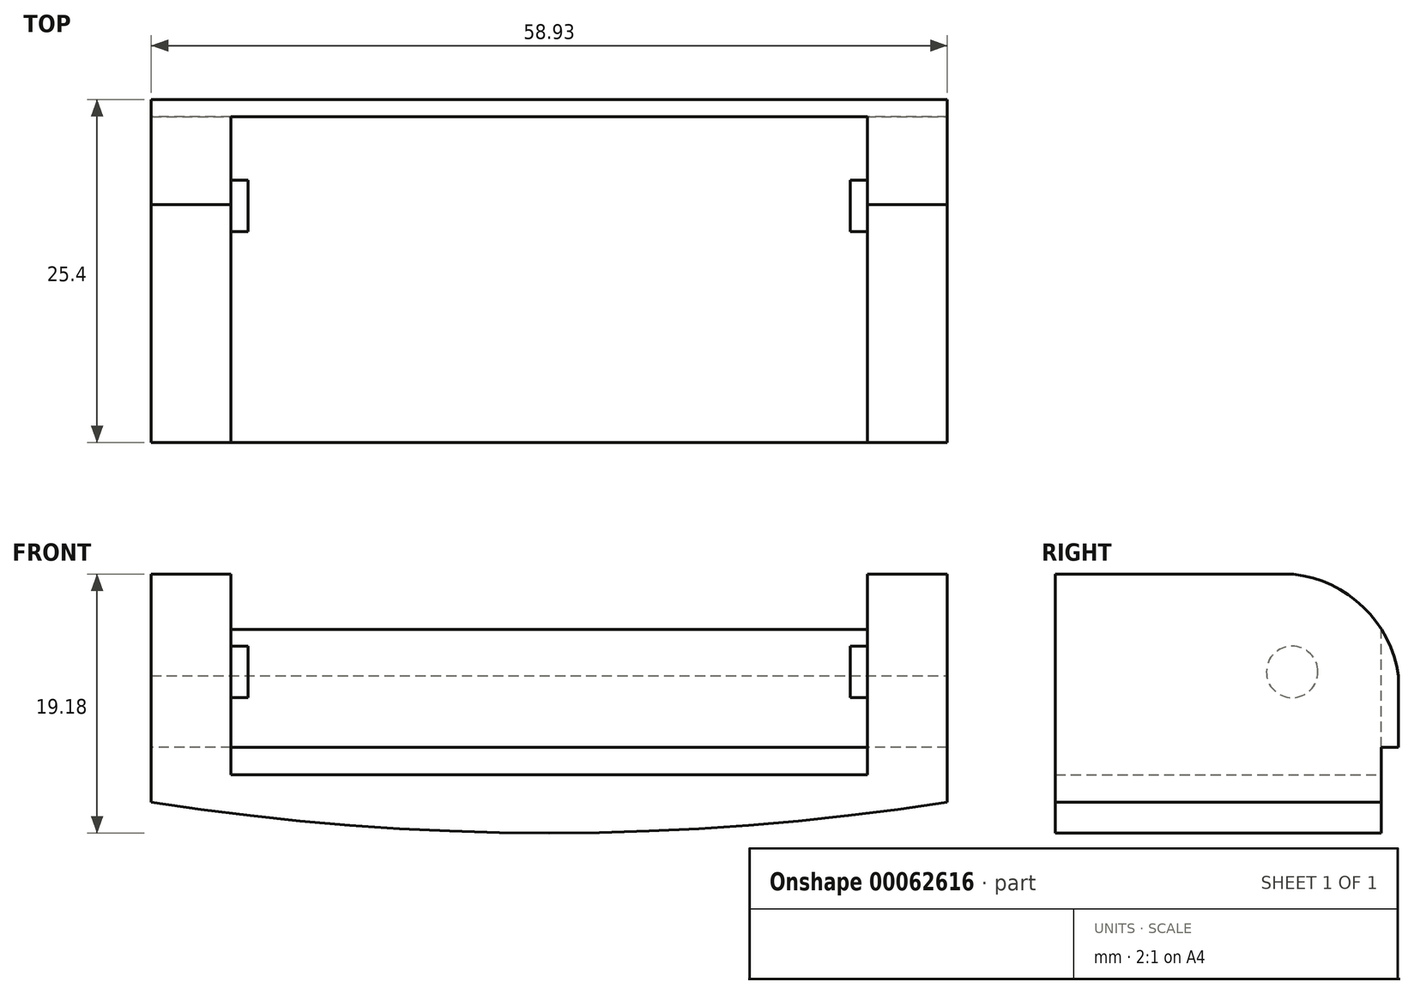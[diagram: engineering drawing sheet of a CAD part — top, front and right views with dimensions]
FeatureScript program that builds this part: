
annotation { "Feature Type Name" : "Feature", "Feature Type Description" : "" }
export const myFeature = defineFeature(function(context is Context, id is Id, definition is map)
    precondition{}
    {
        {
            var Q0;
            Q0=qCreatedBy(makeId("Front.planeOp"),FACE);
            var sketch = newSketch(context, id + "F0", { "sketchPlane" : qUnion([Q0])});
            skLineSegment(sketch, "E0", {"start": v(0, 0) * mm, "end": v(0, 16.9) * mm});
            skLineSegment(sketch, "E1", {"start": v(0, 16.9) * mm, "end": v(-5.9, 16.9) * mm});
            skLineSegment(sketch, "E2", {"start": v(-58.93, 16.9) * mm, "end": v(-58.93, 0) * mm});
            skArc(sketch, "E3", {"start": v(-58.93, 0) * mm, "mid": v(-29.46, -2.29) * mm, "end": v(0, 0) * mm});
            skLineSegment(sketch, "E4", {"start": v(-53.02, 16.9) * mm, "end": v(-53.02, 2.03) * mm});
            skLineSegment(sketch, "E5", {"start": v(-53.02, 2.03) * mm, "end": v(-5.9, 2.03) * mm});
            skLineSegment(sketch, "E6", {"start": v(-5.9, 2.03) * mm, "end": v(-5.9, 16.9) * mm});
            skLineSegment(sketch, "E7.trimOffspring", {"start": v(-53.02, 16.9) * mm, "end": v(-58.93, 16.9) * mm});
            skLineSegment(sketch, "E8", {"start": v(-53.02, 16.9) * mm, "end": v(-5.9, 16.9) * mm});
            skSolve(sketch);
        }
        {
            var Q0;
            Q0=makeQuery(id+"F0.imprint","IMPRINT",FACE,{"disambiguationData":[TD([[makeQuery(id+"F0.imprint","IMPRINT",EDGE,{"derivedFrom":sQuery(id+"F0.wireOp",EDGE,"E0")}),1.0]])]});
            extrude(context, id + "F1", {"entities" : qUnion([Q0]), "depth" : 25.4 * mm});
        }
        {
            var Q0;
            Q0=makeQuery(id+"F0.imprint","IMPRINT",FACE,{"disambiguationData":[TD([[makeQuery(id+"F0.imprint","IMPRINT",EDGE,{"derivedFrom":sQuery(id+"F0.wireOp",EDGE,"E4")}),1.0]])]});
            extrude(context, id + "F2", {"entities" : qUnion([Q0]), "operationType" : NewBodyOperationType.ADD, "depth" : 1.27 * mm});
        }
        {
            var Q0;
            {var subQ0=sQuery(id+"F0.wireOp",EDGE,"E6");var subQ1=sQuery(id+"F0.wireOp",EDGE,"E5");var subQ2=sQuery(id+"F0.wireOp",EDGE,"E4");Q0=makeQuery(id+"F2.boolean.opBoolean","MERGE",FACE,{"derivedFrom":[makeQuery(id+"F1.opExtrude","CAP_FACE",FACE,{"disambiguationData":[OSD([sQuery(id+"F0.wireOp",EDGE,"E0"),sQuery(id+"F0.wireOp",EDGE,"E1"),sQuery(id+"F0.wireOp",EDGE,"E2"),sQuery(id+"F0.wireOp",EDGE,"E3"),subQ2,subQ1,subQ0,sQuery(id+"F0.wireOp",EDGE,"E7.trimOffspring")])],"isStart":true}),makeQuery(id+"F2.opExtrude","CAP_FACE",FACE,{"disambiguationData":[OSD([subQ2,subQ1,subQ0,sQuery(id+"F0.wireOp",EDGE,"E8")])],"isStart":true})]});}
            var sketch = newSketch(context, id + "F3", { "sketchPlane" : qUnion([Q0])});
            skLineSegment(sketch, "E9", {"start": v(0, 4.06) * mm, "end": v(58.93, 4.06) * mm});
            skSolve(sketch);
        }
        {
            var Q0;
            {var subQ0=sQuery(id+"F3.wireOp",EDGE,"E9");Q0=makeQuery(id+"F3.imprint","IMPRINT",FACE,{"disambiguationData":[TD([[makeQuery(id+"F3.imprint","IMPRINT",EDGE,{"derivedFrom":subQ0}),-1.0]])]});}
            extrude(context, id + "F4", {"entities" : qUnion([Q0]), "operationType" : NewBodyOperationType.REMOVE, "oppositeDirection" : true, "depth" : 1.27 * mm});
        }
        {
            var Q0;
            Q0=makeQuery(id+"F1.opExtrude","SWEPT_FACE",FACE,{"disambiguationData":[OSD([sQuery(id+"F0.wireOp",EDGE,"E6")])]});
            var sketch = newSketch(context, id + "F5", { "sketchPlane" : qUnion([Q0])});
            skCircle(sketch, "E10", {"center": v(7.87, 9.65) * mm, "radius": 1.9 * mm});
            skSolve(sketch);
        }
        {
            var Q0;
            Q0=makeQuery(id+"F5.imprint","IMPRINT",FACE,{"disambiguationData":[TD([[makeQuery(id+"F5.imprint","IMPRINT",EDGE,{"derivedFrom":sQuery(id+"F5.wireOp",EDGE,"E10")}),1.0]])]});
            extrude(context, id + "F6", {"entities" : qUnion([Q0]), "operationType" : NewBodyOperationType.ADD, "depth" : 1.27 * mm});
        }
        {
            var Q0;
            Q0=makeQuery(id+"F1.opExtrude","SWEPT_FACE",FACE,{"disambiguationData":[OSD([sQuery(id+"F0.wireOp",EDGE,"E4")])]});
            var sketch = newSketch(context, id + "F7", { "sketchPlane" : qUnion([Q0])});
            skCircle(sketch, "E11", {"center": v(-7.87, 9.65) * mm, "radius": 1.9 * mm});
            skSolve(sketch);
        }
        {
            var Q0;
            Q0=makeQuery(id+"F7.imprint","IMPRINT",FACE,{"disambiguationData":[TD([[makeQuery(id+"F7.imprint","IMPRINT",EDGE,{"derivedFrom":sQuery(id+"F7.wireOp",EDGE,"E11")}),1.0]])]});
            extrude(context, id + "F8", {"entities" : qUnion([Q0]), "operationType" : NewBodyOperationType.ADD, "depth" : 1.27 * mm});
        }
        {
            var Q0;
            Q0=makeQuery(id+"F1.opExtrude","SWEPT_FACE",FACE,{"disambiguationData":[OSD([sQuery(id+"F0.wireOp",EDGE,"E0")])]});
            var sketch = newSketch(context, id + "F9", { "sketchPlane" : qUnion([Q0])});
            skArc(sketch, "E12", {"start": v(0, 6.82) * mm, "mid": v(-2.4, 14.25) * mm, "end": v(-9.74, 16.9) * mm});
            skSolve(sketch);
        }
        {
            var Q0;
            {var subQ0=sQuery(id+"F9.wireOp",EDGE,"E12");var subQ1=sQuery(id+"F0.wireOp",EDGE,"E0");var subQ2=makeQuery(id+"F1.opExtrude","CAP_EDGE",EDGE,{"disambiguationData":[OSD([subQ1])],"isStart":true});var subQ3=makeQuery(id+"F9.imprint","INTERSECT",VERTEX,{"disambiguationData":[OD(1.0)],"derivedFrom":[subQ2,subQ0]});Q0=makeQuery(id+"F9.imprint","IMPRINT",FACE,{"disambiguationData":[TD([[makeQuery(id+"F9.imprint","IMPRINT",EDGE,{"disambiguationData":[TD([[subQ3,-1.0]])],"derivedFrom":subQ0}),-1.0]])]});}
            extrude(context, id + "F10", {"entities" : qUnion([Q0]), "operationType" : NewBodyOperationType.REMOVE, "oppositeDirection" : true, "depth" : 63.5 * mm});
        }
    });
